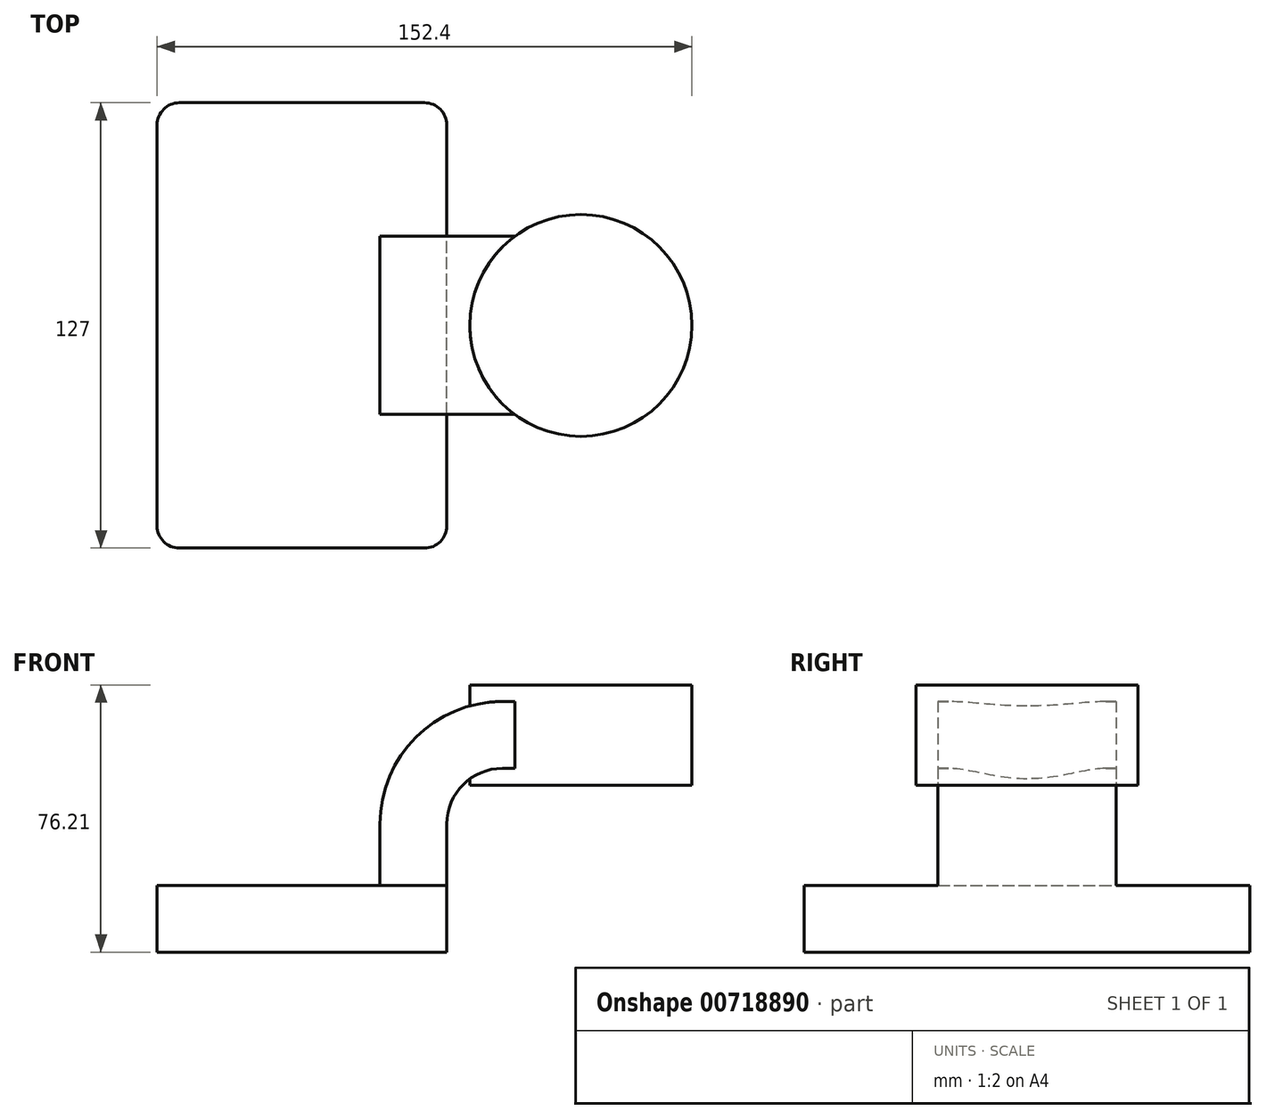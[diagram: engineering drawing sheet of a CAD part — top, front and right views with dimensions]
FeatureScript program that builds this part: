
annotation { "Feature Type Name" : "Feature", "Feature Type Description" : "" }
export const myFeature = defineFeature(function(context is Context, id is Id, definition is map)
    precondition{}
    {
        {
            var Q0;
            Q0=qCreatedBy(makeId("Front.planeOp"),FACE);
            var sketch = newSketch(context, id + "F0", { "sketchPlane" : qUnion([Q0])});
            skLineSegment(sketch, "E0.bottom", {"start": v(-41.28, 9.52) * mm, "end": v(41.27, 9.53) * mm});
            skLineSegment(sketch, "E0.top", {"start": v(-41.28, -9.52) * mm, "end": v(41.28, -9.52) * mm});
            skLineSegment(sketch, "E0.left", {"start": v(-41.28, 9.52) * mm, "end": v(-41.28, -9.53) * mm});
            skLineSegment(sketch, "E0.right", {"start": v(41.27, 9.53) * mm, "end": v(41.28, -9.52) * mm});
            skPoint(sketch, "E0.middle", {"position": v(0, 0) * mm});
            skLineSegment(sketch, "E1.bottom", {"start": v(60.32, 66.68) * mm, "end": v(111.12, 66.68) * mm});
            skLineSegment(sketch, "E1.top", {"start": v(60.32, 38.1) * mm, "end": v(111.12, 38.1) * mm});
            skLineSegment(sketch, "E1.left", {"start": v(60.32, 66.68) * mm, "end": v(60.32, 38.1) * mm});
            skLineSegment(sketch, "E1.right", {"start": v(111.12, 66.68) * mm, "end": v(111.12, 38.1) * mm});
            skPoint(sketch, "E1.middle", {"position": v(85.72, 52.39) * mm});
            skLineSegment(sketch, "E2", {"start": v(41.27, 9.53) * mm, "end": v(41.27, 27) * mm});
            skArc(sketch, "E3", {"start": v(41.27, 27) * mm, "mid": v(45.92, 38.23) * mm, "end": v(57.15, 42.88) * mm});
            skLineSegment(sketch, "E4", {"start": v(57.15, 42.88) * mm, "end": v(79.49, 42.88) * mm});
            skLineSegment(sketch, "E5.0", {"start": v(57.15, 61.93) * mm, "end": v(79.49, 61.93) * mm});
            skArc(sketch, "E5.1", {"start": v(22.22, 27) * mm, "mid": v(32.45, 51.7) * mm, "end": v(57.15, 61.93) * mm});
            skLineSegment(sketch, "E5.2", {"start": v(22.22, 9.53) * mm, "end": v(22.22, 27) * mm});
            skLineSegment(sketch, "E6", {"start": v(79.49, 38.1) * mm, "end": v(79.49, 66.68) * mm});
            skFitSpline(sketch, "E7", {"points": [v(-41.28, 9.53) * mm, v(57.15, 61.93) * mm], "startDerivative": vector(63.86, 100.16) * mm, "endDerivative": vector(104.3, -18.59) * mm});
            skSolve(sketch);
        }
        {
            var Q0;
            Q0=makeQuery(id+"F0.imprint","IMPRINT",FACE,{"disambiguationData":[TD([[makeQuery(id+"F0.imprint","IMPRINT",EDGE,{"derivedFrom":sQuery(id+"F0.wireOp",EDGE,"E0.top")}),1.0]])]});
            extrude(context, id + "F1", {"entities" : qUnion([Q0]), "endBound" : BoundingType.SYMMETRIC, "depth" : 127 * mm, "offsetDistance" : 25.4 * mm});
        }
        {
            var Q0;
            {var subQ1=sQuery(id+"F0.wireOp",EDGE,"E2");Q0=makeQuery(id+"F0.imprint","IMPRINT",FACE,{"disambiguationData":[TD([[makeQuery(id+"F0.imprint","IMPRINT",EDGE,{"derivedFrom":subQ1}),1.0]])]});}
            var Q1;
            {var subQ0=sQuery(id+"F0.wireOp",EDGE,"E5.0");var subQ1=sQuery(id+"F0.wireOp",EDGE,"E1.left");var subQ2=makeQuery(id+"F0.imprint","INTERSECT",VERTEX,{"derivedFrom":[subQ1,subQ0]});Q1=makeQuery(id+"F0.imprint","IMPRINT",FACE,{"disambiguationData":[TD([[makeQuery(id+"F0.imprint","IMPRINT",EDGE,{"disambiguationData":[TD([[subQ2,-1.0]])],"derivedFrom":subQ1}),1.0]])]});}
            extrude(context, id + "F2", {"entities" : qUnion([Q0, Q1]), "operationType" : NewBodyOperationType.ADD, "endBound" : BoundingType.SYMMETRIC, "depth" : 50.8 * mm, "offsetDistance" : 25.4 * mm});
        }
        {
            var Q0;
            Q0=makeQuery(id+"F0.imprint","IMPRINT",FACE,{"disambiguationData":[TD([[makeQuery(id+"F0.imprint","IMPRINT",EDGE,{"derivedFrom":sQuery(id+"F0.wireOp",EDGE,"E5.1")}),1.0]])]});
            extrude(context, id + "F3", {"entities" : qUnion([Q0]), "operationType" : NewBodyOperationType.ADD, "endBound" : BoundingType.SYMMETRIC, "depth" : 15.88 * mm, "offsetDistance" : 25.4 * mm});
        }
        {
            var Q0;
            Q0=makeQuery(id+"F1.opExtrude","CAP_EDGE",EDGE,{"disambiguationData":[OSD([sQuery(id+"F0.wireOp",EDGE,"E0.left")])],"isStart":false});
            var Q1;
            Q1=makeQuery(id+"F1.opExtrude","CAP_EDGE",EDGE,{"disambiguationData":[OSD([sQuery(id+"F0.wireOp",EDGE,"E0.right")])],"isStart":false});
            var Q2;
            Q2=makeQuery(id+"F1.opExtrude","CAP_EDGE",EDGE,{"disambiguationData":[OSD([sQuery(id+"F0.wireOp",EDGE,"E0.right")])],"isStart":true});
            var Q3;
            Q3=makeQuery(id+"F1.opExtrude","CAP_EDGE",EDGE,{"disambiguationData":[OSD([sQuery(id+"F0.wireOp",EDGE,"E0.left")])],"isStart":true});
            fillet(context, id + "F4", {"entities" : qUnion([Q0, Q1, Q2, Q3]), "radius" : 6.35 * mm, "tangentPropagation" : true, "allowEdgeOverflow" : false});
        }
        {
            var Q0;
            {var subQ0=sQuery(id+"F0.wireOp",EDGE,"E1.right");Q0=makeQuery(id+"F0.imprint","IMPRINT",FACE,{"disambiguationData":[TD([[makeQuery(id+"F0.imprint","IMPRINT",EDGE,{"derivedFrom":subQ0}),-1.0]])]});}
            var Q1;
            Q1=sQuery(id+"F0.wireOp",EDGE,"E6");
            revolve(context, id + "F5", {"operationType" : NewBodyOperationType.ADD, "surfaceOperationType" : NewSurfaceOperationType.NEW, "entities" : qUnion([Q0]), "axis" : qUnion([Q1]), "revolveType" : RevolveType.FULL});
        }
    });
